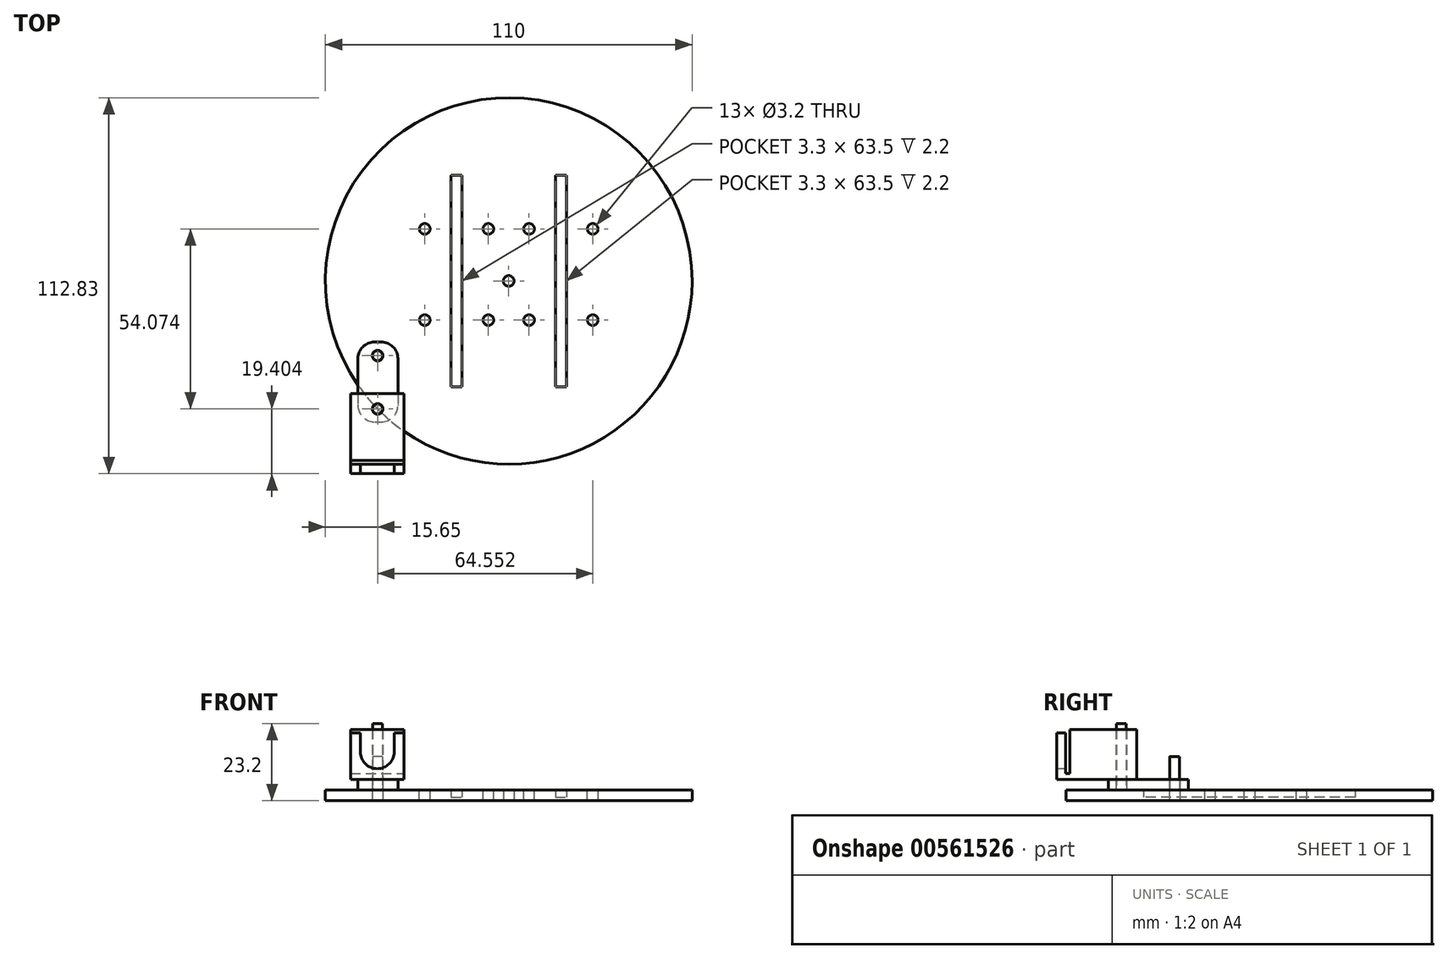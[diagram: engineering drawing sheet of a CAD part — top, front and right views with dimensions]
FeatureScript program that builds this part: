
annotation { "Feature Type Name" : "Feature", "Feature Type Description" : "" }
export const myFeature = defineFeature(function(context is Context, id is Id, definition is map)
    precondition{}
    {
        {
            var Q0;
            Q0=qCreatedBy(makeId("Top.planeOp"),FACE);
            var sketch = newSketch(context, id + "F0", { "sketchPlane" : qUnion([Q0])});
            skCircle(sketch, "E0", {"center": v(39.35, 117.44) * mm, "radius": 55 * mm});
            skCircle(sketch, "E1", {"center": v(0, 95.01) * mm, "radius": 1.6 * mm});
            skCircle(sketch, "E2", {"center": v(39.35, 117.44) * mm, "radius": 1.6 * mm});
            skLineSegment(sketch, "E3.bottom", {"start": v(22.05, 149.19) * mm, "end": v(25.35, 149.19) * mm});
            skLineSegment(sketch, "E3.top", {"start": v(22.05, 85.69) * mm, "end": v(25.35, 85.69) * mm});
            skLineSegment(sketch, "E3.left", {"start": v(22.05, 149.19) * mm, "end": v(22.05, 85.69) * mm});
            skLineSegment(sketch, "E3.right", {"start": v(25.35, 149.19) * mm, "end": v(25.35, 85.69) * mm});
            skLineSegment(sketch, "E4.bottom", {"start": v(53.35, 149.19) * mm, "end": v(56.65, 149.19) * mm});
            skLineSegment(sketch, "E4.top", {"start": v(53.35, 85.69) * mm, "end": v(56.65, 85.69) * mm});
            skLineSegment(sketch, "E4.left", {"start": v(53.35, 149.19) * mm, "end": v(53.35, 85.69) * mm});
            skLineSegment(sketch, "E4.right", {"start": v(56.65, 149.19) * mm, "end": v(56.65, 85.69) * mm});
            skSolve(sketch);
        }
        {
            var Q0;
            Q0=makeQuery(id+"F0.imprint","IMPRINT",FACE,{"disambiguationData":[TD([[makeQuery(id+"F0.imprint","IMPRINT",EDGE,{"derivedFrom":sQuery(id+"F0.wireOp",EDGE,"E0")}),1.0]])]});
            extrude(context, id + "F1", {"entities" : qUnion([Q0]), "depth" : 3.2 * mm});
        }
        {
            var Q0;
            Q0=makeQuery(id+"F0.imprint","IMPRINT",FACE,{"disambiguationData":[TD([[makeQuery(id+"F0.imprint","IMPRINT",EDGE,{"derivedFrom":sQuery(id+"F0.wireOp",EDGE,"E3.bottom")}),-1.0]])]});
            var Q1;
            Q1=makeQuery(id+"F0.imprint","IMPRINT",FACE,{"disambiguationData":[TD([[makeQuery(id+"F0.imprint","IMPRINT",EDGE,{"derivedFrom":sQuery(id+"F0.wireOp",EDGE,"E4.bottom")}),-1.0]])]});
            extrude(context, id + "F2", {"entities" : qUnion([Q0, Q1]), "operationType" : NewBodyOperationType.ADD, "depth" : 1 * mm});
        }
        {
            var Q0;
            Q0=makeQuery(id+"F1.opExtrude","CAP_FACE",FACE,{"disambiguationData":[OSD([sQuery(id+"F0.wireOp",EDGE,"E0"),sQuery(id+"F0.wireOp",EDGE,"E1"),sQuery(id+"F0.wireOp",EDGE,"E2"),sQuery(id+"F0.wireOp",EDGE,"E3.bottom"),sQuery(id+"F0.wireOp",EDGE,"E3.top"),sQuery(id+"F0.wireOp",EDGE,"E3.left"),sQuery(id+"F0.wireOp",EDGE,"E3.right"),sQuery(id+"F0.wireOp",EDGE,"E4.bottom"),sQuery(id+"F0.wireOp",EDGE,"E4.top"),sQuery(id+"F0.wireOp",EDGE,"E4.left"),sQuery(id+"F0.wireOp",EDGE,"E4.right")])],"isStart":false});
            var sketch = newSketch(context, id + "F3", { "sketchPlane" : qUnion([Q0])});
            skCircle(sketch, "E5", {"center": v(0, 95.01) * mm, "radius": 1.5 * mm});
            skSolve(sketch);
        }
        {
            var Q0;
            Q0=makeQuery(id+"F3.imprint","IMPRINT",FACE,{"disambiguationData":[TD([[makeQuery(id+"F3.imprint","IMPRINT",EDGE,{"derivedFrom":sQuery(id+"F3.wireOp",EDGE,"E5")}),1.0]])]});
            extrude(context, id + "F4", {"entities" : qUnion([Q0]), "depth" : 10 * mm, "offsetDistance" : 25 * mm});
        }
        {
            var Q0;
            Q0=makeQuery(id+"F1.opExtrude","CAP_FACE",FACE,{"disambiguationData":[OSD([sQuery(id+"F0.wireOp",EDGE,"E0"),sQuery(id+"F0.wireOp",EDGE,"E1"),sQuery(id+"F0.wireOp",EDGE,"E2"),sQuery(id+"F0.wireOp",EDGE,"E3.bottom"),sQuery(id+"F0.wireOp",EDGE,"E3.top"),sQuery(id+"F0.wireOp",EDGE,"E3.left"),sQuery(id+"F0.wireOp",EDGE,"E3.right"),sQuery(id+"F0.wireOp",EDGE,"E4.bottom"),sQuery(id+"F0.wireOp",EDGE,"E4.top"),sQuery(id+"F0.wireOp",EDGE,"E4.left"),sQuery(id+"F0.wireOp",EDGE,"E4.right")])],"isStart":false});
            var sketch = newSketch(context, id + "F5", { "sketchPlane" : qUnion([Q0])});
            skLineSegment(sketch, "E6.bottom", {"start": v(-5.9, 99.11) * mm, "end": v(6.1, 99.11) * mm});
            skLineSegment(sketch, "E6.top", {"start": v(-5.9, 75.11) * mm, "end": v(6.1, 75.11) * mm});
            skLineSegment(sketch, "E6.left", {"start": v(-5.9, 99.11) * mm, "end": v(-5.9, 75.11) * mm});
            skLineSegment(sketch, "E6.right", {"start": v(6.1, 99.11) * mm, "end": v(6.1, 75.11) * mm});
            skCircle(sketch, "E7", {"center": v(0, 95.01) * mm, "radius": 1.6 * mm});
            skCircle(sketch, "E8", {"center": v(0, 79.01) * mm, "radius": 1.6 * mm});
            skSolve(sketch);
        }
        {
            var Q0;
            {var subQ4=sQuery(id+"F5.wireOp",EDGE,"E6.top");var subQ6=sQuery(id+"F5.wireOp",EDGE,"E6.left");var subQ7=makeQuery(id+"F5.imprint","INTERSECT",VERTEX,{"derivedFrom":[subQ4,subQ6]});Q0=makeQuery(id+"F5.imprint","IMPRINT",FACE,{"disambiguationData":[TD([[makeQuery(id+"F5.imprint","IMPRINT",EDGE,{"disambiguationData":[TD([[subQ7,-1.0]])],"derivedFrom":subQ4}),1.0]])]});}
            var Q1;
            {var subQ1=sQuery(id+"F5.wireOp",EDGE,"E6.bottom");Q1=makeQuery(id+"F5.imprint","IMPRINT",FACE,{"disambiguationData":[TD([[makeQuery(id+"F5.imprint","IMPRINT",EDGE,{"derivedFrom":subQ1}),-1.0]])]});}
            extrude(context, id + "F6", {"entities" : qUnion([Q0, Q1]), "depth" : 3.2 * mm, "offsetDistance" : 25 * mm});
        }
        {
            var Q0;
            Q0=makeQuery(id+"F6.opExtrude","SWEPT_EDGE",EDGE,{"disambiguationData":[OSD([sQuery(id+"F5.wireOp",EDGE,"E6.bottom"),sQuery(id+"F5.wireOp",EDGE,"E6.left")])]});
            var Q1;
            Q1=makeQuery(id+"F6.opExtrude","SWEPT_EDGE",EDGE,{"disambiguationData":[OSD([sQuery(id+"F5.wireOp",EDGE,"E6.bottom"),sQuery(id+"F5.wireOp",EDGE,"E6.right")])]});
            var Q2;
            Q2=makeQuery(id+"F6.opExtrude","SWEPT_EDGE",EDGE,{"disambiguationData":[OSD([sQuery(id+"F5.wireOp",EDGE,"E6.top"),sQuery(id+"F5.wireOp",EDGE,"E6.right")])]});
            var Q3;
            Q3=makeQuery(id+"F6.opExtrude","SWEPT_EDGE",EDGE,{"disambiguationData":[OSD([sQuery(id+"F5.wireOp",EDGE,"E6.top"),sQuery(id+"F5.wireOp",EDGE,"E6.left")])]});
            fillet(context, id + "F7", {"entities" : qUnion([Q0, Q1, Q2, Q3]), "radius" : 5 * mm, "tangentPropagation" : true, "allowEdgeOverflow" : false});
        }
        {
            var Q0;
            Q0=makeQuery(id+"F1.opExtrude","CAP_FACE",FACE,{"disambiguationData":[OSD([sQuery(id+"F0.wireOp",EDGE,"E0"),sQuery(id+"F0.wireOp",EDGE,"E1"),sQuery(id+"F0.wireOp",EDGE,"E2"),sQuery(id+"F0.wireOp",EDGE,"E3.bottom"),sQuery(id+"F0.wireOp",EDGE,"E3.top"),sQuery(id+"F0.wireOp",EDGE,"E3.left"),sQuery(id+"F0.wireOp",EDGE,"E3.right"),sQuery(id+"F0.wireOp",EDGE,"E4.bottom"),sQuery(id+"F0.wireOp",EDGE,"E4.top"),sQuery(id+"F0.wireOp",EDGE,"E4.left"),sQuery(id+"F0.wireOp",EDGE,"E4.right")])],"isStart":false});
            var sketch = newSketch(context, id + "F8", { "sketchPlane" : qUnion([Q0])});
            skCircle(sketch, "E9", {"center": v(0, 79.01) * mm, "radius": 1.5 * mm});
            skSolve(sketch);
        }
        {
            var Q0;
            {var subQ0=sQuery(id+"F8.wireOp",EDGE,"E9");var subQ1=makeQuery(id+"F1.opExtrude","CAP_EDGE",EDGE,{"disambiguationData":[OSD([sQuery(id+"F0.wireOp",EDGE,"E0")])],"isStart":false});var subQ2=makeQuery(id+"F8.imprint","INTERSECT",VERTEX,{"disambiguationData":[OD(0.0)],"derivedFrom":[subQ1,subQ0]});Q0=makeQuery(id+"F8.imprint","IMPRINT",FACE,{"disambiguationData":[TD([[makeQuery(id+"F8.imprint","IMPRINT",EDGE,{"disambiguationData":[TD([[subQ2,-1.0]])],"derivedFrom":subQ0}),1.0]])]});}
            var Q1;
            {var subQ0=sQuery(id+"F8.wireOp",EDGE,"E9");var subQ1=makeQuery(id+"F1.opExtrude","CAP_EDGE",EDGE,{"disambiguationData":[OSD([sQuery(id+"F0.wireOp",EDGE,"E0")])],"isStart":false});var subQ2=makeQuery(id+"F8.imprint","INTERSECT",VERTEX,{"disambiguationData":[OD(0.0)],"derivedFrom":[subQ1,subQ0]});Q1=makeQuery(id+"F8.imprint","IMPRINT",FACE,{"disambiguationData":[TD([[makeQuery(id+"F8.imprint","IMPRINT",EDGE,{"disambiguationData":[TD([[subQ2,1.0]])],"derivedFrom":subQ0}),1.0]])]});}
            extrude(context, id + "F9", {"entities" : qUnion([Q0, Q1]), "depth" : 20 * mm, "offsetDistance" : 25 * mm});
        }
        {
            var Q0;
            Q0=makeQuery(id+"F6.opExtrude","CAP_FACE",FACE,{"disambiguationData":[OSD([sQuery(id+"F5.wireOp",EDGE,"E6.bottom"),sQuery(id+"F5.wireOp",EDGE,"E6.top"),sQuery(id+"F5.wireOp",EDGE,"E6.left"),sQuery(id+"F5.wireOp",EDGE,"E6.right"),sQuery(id+"F5.wireOp",EDGE,"E7"),sQuery(id+"F5.wireOp",EDGE,"E8")])],"isStart":false});
            var sketch = newSketch(context, id + "F10", { "sketchPlane" : qUnion([Q0])});
            skLineSegment(sketch, "E10.bottom", {"start": v(-8.1, 83.61) * mm, "end": v(7.9, 83.61) * mm});
            skLineSegment(sketch, "E10.top", {"start": v(-8.1, 59.61) * mm, "end": v(7.9, 59.61) * mm});
            skLineSegment(sketch, "E10.left", {"start": v(-8.1, 83.61) * mm, "end": v(-8.1, 59.61) * mm});
            skLineSegment(sketch, "E10.right", {"start": v(7.9, 83.61) * mm, "end": v(7.9, 59.61) * mm});
            skCircle(sketch, "E11", {"center": v(0, 79.01) * mm, "radius": 1.6 * mm});
            skSolve(sketch);
        }
        {
            var Q0;
            Q0=makeQuery(id+"F10.imprint","IMPRINT",FACE,{"disambiguationData":[TD([[makeQuery(id+"F10.imprint","IMPRINT",EDGE,{"derivedFrom":sQuery(id+"F10.wireOp",EDGE,"E10.top")}),1.0]])]});
            var Q1;
            Q1=makeQuery(id+"F10.imprint","IMPRINT",FACE,{"disambiguationData":[TD([[makeQuery(id+"F10.imprint","IMPRINT",EDGE,{"derivedFrom":sQuery(id+"F10.wireOp",EDGE,"E11")}),-1.0]])]});
            extrude(context, id + "F11", {"entities" : qUnion([Q0, Q1]), "depth" : 15 * mm, "offsetDistance" : 25 * mm});
        }
        {
            var Q0;
            Q0=makeQuery(id+"F11.opExtrude","SWEPT_FACE",FACE,{"disambiguationData":[OSD([sQuery(id+"F10.wireOp",EDGE,"E10.right")])]});
            var sketch = newSketch(context, id + "F12", { "sketchPlane" : qUnion([Q0])});
            skLineSegment(sketch, "E12.bottom", {"start": v(59.61, 21.4) * mm, "end": v(63.61, 21.4) * mm});
            skLineSegment(sketch, "E12.right", {"start": v(63.61, 21.4) * mm, "end": v(63.61, 8.2) * mm});
            skLineSegment(sketch, "E13.top", {"start": v(59.61, 20.4) * mm, "end": v(62.36, 20.4) * mm});
            skLineSegment(sketch, "E13.right", {"start": v(62.36, 8.2) * mm, "end": v(62.36, 20.4) * mm});
            skLineSegment(sketch, "E14", {"start": v(62.36, 8.2) * mm, "end": v(63.61, 8.2) * mm});
            skLineSegment(sketch, "E15", {"start": v(59.61, 21.4) * mm, "end": v(59.61, 20.4) * mm});
            skSolve(sketch);
        }
        {
            var Q0;
            Q0=makeQuery(id+"F12.imprint","IMPRINT",FACE,{"disambiguationData":[TD([[makeQuery(id+"F12.imprint","IMPRINT",EDGE,{"derivedFrom":sQuery(id+"F12.wireOp",EDGE,"E12.bottom")}),1.0]])]});
            extrude(context, id + "F13", {"entities" : qUnion([Q0]), "operationType" : NewBodyOperationType.REMOVE, "oppositeDirection" : true, "depth" : 25 * mm, "offsetDistance" : 25 * mm});
        }
        {
            var Q0;
            Q0=makeQuery(id+"F1.opExtrude","CAP_FACE",FACE,{"disambiguationData":[OSD([sQuery(id+"F0.wireOp",EDGE,"E0"),sQuery(id+"F0.wireOp",EDGE,"E1"),sQuery(id+"F0.wireOp",EDGE,"E2"),sQuery(id+"F0.wireOp",EDGE,"E3.bottom"),sQuery(id+"F0.wireOp",EDGE,"E3.top"),sQuery(id+"F0.wireOp",EDGE,"E3.left"),sQuery(id+"F0.wireOp",EDGE,"E3.right"),sQuery(id+"F0.wireOp",EDGE,"E4.bottom"),sQuery(id+"F0.wireOp",EDGE,"E4.top"),sQuery(id+"F0.wireOp",EDGE,"E4.left"),sQuery(id+"F0.wireOp",EDGE,"E4.right")])],"isStart":false});
            var sketch = newSketch(context, id + "F14", { "sketchPlane" : qUnion([Q0])});
            skCircle(sketch, "E16", {"center": v(64.55, 105.69) * mm, "radius": 1.6 * mm});
            skCircle(sketch, "E17", {"center": v(64.55, 133.09) * mm, "radius": 1.6 * mm});
            skCircle(sketch, "E18", {"center": v(45.45, 133.09) * mm, "radius": 1.6 * mm});
            skCircle(sketch, "E19", {"center": v(45.45, 105.69) * mm, "radius": 1.6 * mm});
            skCircle(sketch, "E20", {"center": v(33.25, 105.69) * mm, "radius": 1.6 * mm});
            skCircle(sketch, "E21", {"center": v(33.25, 133.09) * mm, "radius": 1.6 * mm});
            skCircle(sketch, "E22", {"center": v(14.15, 133.09) * mm, "radius": 1.6 * mm});
            skCircle(sketch, "E23", {"center": v(14.15, 105.69) * mm, "radius": 1.6 * mm});
            skSolve(sketch);
        }
        {
            var Q0;
            Q0 = qSketchRegion(id + "F14", true);
            extrude(context, id + "F15", {"entities" : qUnion([Q0]), "operationType" : NewBodyOperationType.REMOVE, "oppositeDirection" : true, "depth" : 8 * mm, "offsetDistance" : 25 * mm});
        }
        {
            var Q0;
            Q0=makeQuery(id+"F11.opExtrude","SWEPT_FACE",FACE,{"disambiguationData":[OSD([sQuery(id+"F10.wireOp",EDGE,"E10.top")])]});
            var sketch = newSketch(context, id + "F16", { "sketchPlane" : qUnion([Q0])});
            skLineSegment(sketch, "E24", {"start": v(-0.1, 20.4) * mm, "end": v(-0.1, 6.4) * mm, "construction": true});
            skLineSegment(sketch, "E25", {"start": v(-8.1, 13.4) * mm, "end": v(7.9, 13.4) * mm, "construction": true});
            skLineSegment(sketch, "E26", {"start": v(-8.1, 14.7) * mm, "end": v(7.9, 14.7) * mm, "construction": true});
            skArc(sketch, "E27", {"start": v(-5.2, 14.7) * mm, "mid": v(-0.1, 9.62) * mm, "end": v(5, 14.7) * mm});
            skPoint(sketch, "E27.startSnap0", {"position": v(-5.2, 15.2) * mm});
            skLineSegment(sketch, "E28", {"start": v(-5.2, 14.7) * mm, "end": v(-5.2, 20.4) * mm});
            skLineSegment(sketch, "E29", {"start": v(5, 14.7) * mm, "end": v(5, 20.4) * mm});
            skSolve(sketch);
        }
        {
            var Q0;
            Q0=makeQuery(id+"F16.imprint","IMPRINT",FACE,{"disambiguationData":[TD([[makeQuery(id+"F16.imprint","IMPRINT",EDGE,{"derivedFrom":sQuery(id+"F16.wireOp",EDGE,"E27")}),1.0]])]});
            extrude(context, id + "F17", {"entities" : qUnion([Q0]), "operationType" : NewBodyOperationType.REMOVE, "oppositeDirection" : true, "depth" : 2.75 * mm, "offsetDistance" : 25 * mm});
        }
    });
